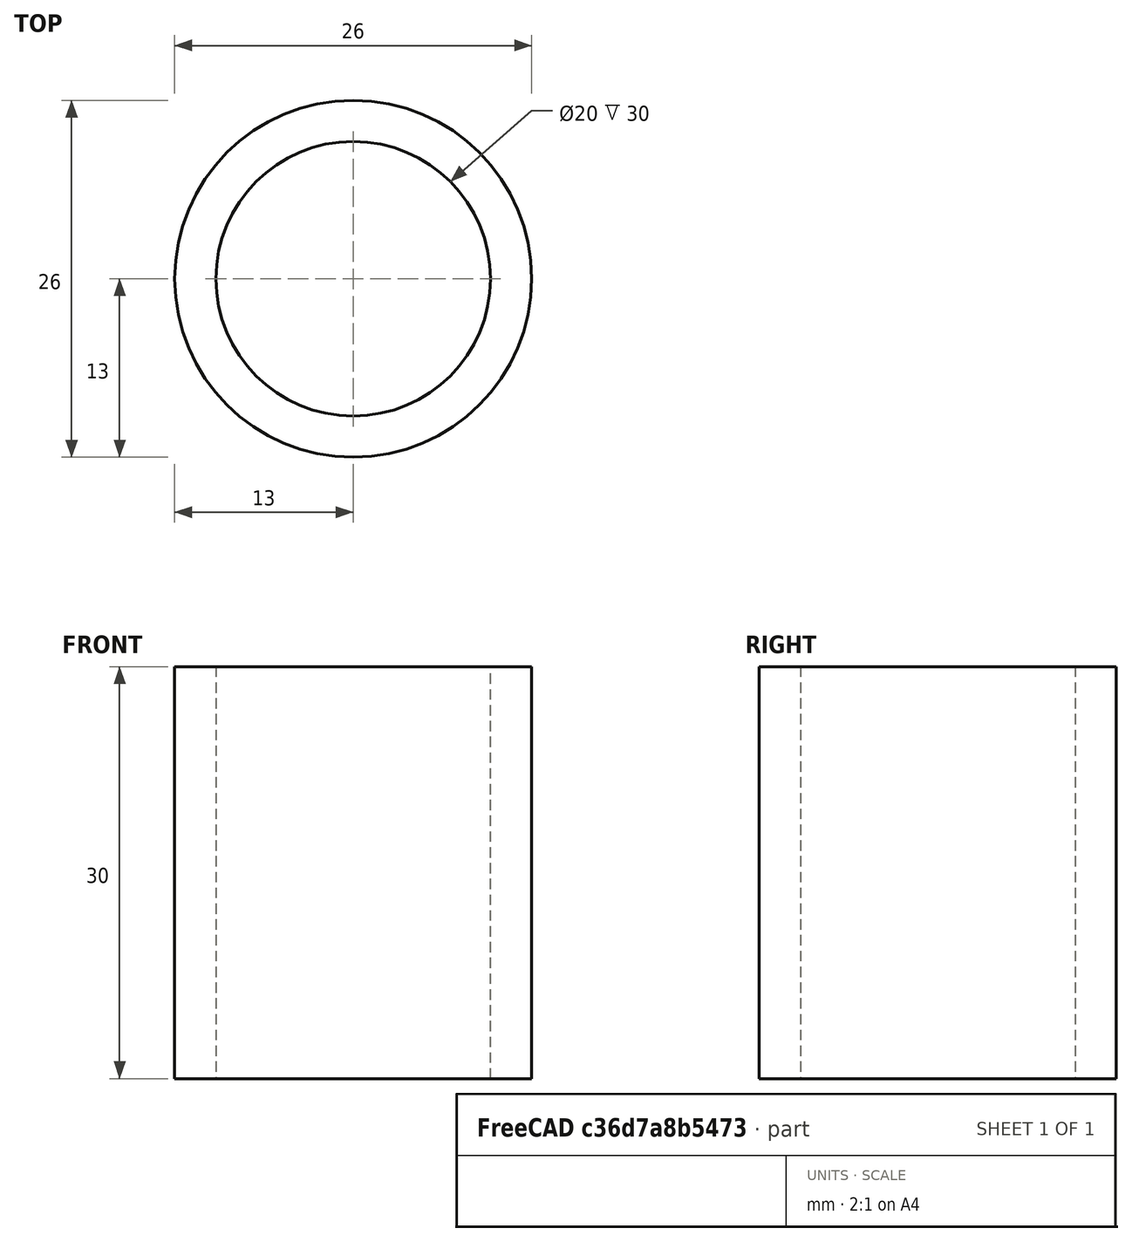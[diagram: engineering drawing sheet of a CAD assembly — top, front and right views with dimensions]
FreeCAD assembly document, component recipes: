
FREECAD ASSEMBLY — COMPONENT RECIPES ("Assembly_file")

This assembly document has 2 components, labeled P0..P1 below (a component is one placed body or linked part). 2 of them carry a construction recipe — the FreeCAD feature program that regenerates the part from scratch, quoted from this document or its linked companion documents; the rest are supplied as boundary geometry only. No exploded tour is included for this assembly.
COMPONENT P0 — recipe-attached ("Body_part_in", modeled in this document).
Construction recipe (the document's own serialized feature program — sketch geometry with constraints, then the solid features built on it; lengths are millimeters unless a unit is written):

FEATURE [Sketcher::SketchObject] Sketch
  FullyConstrained = true
  MapMode = 5
  Support = -> [XY_Plane001]
  sketch-geometry (1):
    g0: Circle CenterX=0 CenterY=0 CenterZ=0 NormalX=0 NormalY=0 NormalZ=1 AngleXU=0 Radius=10
  constraints (2):
    c: Coincident(g0,g-1)
    c: Diameter(g0) = 20
FEATURE [PartDesign::Pad] Pad
  Direction = (1,1,1)
  Length = 30
  Length2 = 100
  Profile = -> Sketch
  Type = 0
FEATURE [PartDesign::CoordinateSystem] LCS_in
  AttacherType = Attacher::AttachEngine3D
  MapMode = 11
  Placement = pos=(0,0,0) rot=(0,0,1;1.5708rad)
  Support = -> [Pad]
FEATURE [PartDesign::Body] Body  label="Body_part_in"
  Group = -> [Sketch,Pad,LCS_in]
  Origin = -> Origin001
  Tip = -> Pad
COMPONENT P1 — recipe-attached ("Body_part_out", modeled in this document).
Construction recipe (the document's own serialized feature program — sketch geometry with constraints, then the solid features built on it; lengths are millimeters unless a unit is written):

FEATURE [Sketcher::SketchObject] Sketch001
  FullyConstrained = true
  MapMode = 5
  Support = -> [XY_Plane002]
  sketch-geometry (1):
    g0: Circle CenterX=0 CenterY=0 CenterZ=0 NormalX=0 NormalY=0 NormalZ=1 AngleXU=0 Radius=10
  constraints (2):
    c: Coincident(g0,g-1)
    c: Diameter(g0) = 20
FEATURE [Sketcher::SketchObject] Sketch002
  FullyConstrained = true
  MapMode = 5
  Support = -> [XY_Plane002]
  sketch-geometry (1):
    g0: Circle CenterX=0 CenterY=0 CenterZ=0 NormalX=0 NormalY=0 NormalZ=1 AngleXU=0 Radius=13
  constraints (2):
    c: Coincident(g0,g-1)
    c: Diameter(g0) = 26
FEATURE [PartDesign::Pad] Pad001
  Direction = (1,1,1)
  Length = 30
  Length2 = 100
  Profile = -> Sketch002
  Type = 0
FEATURE [PartDesign::Pocket] Pocket
  BaseFeature = -> Pad001
  Length = 5
  Length2 = 100
  Profile = -> Sketch001
  Reversed = true
  Type = 1
FEATURE [PartDesign::CoordinateSystem] LCS_out
  AttacherType = Attacher::AttachEngine3D
  MapMode = 11
  Placement = pos=(0,0,0) rot=(0,0,1;1.5708rad)
  Support = -> [Pocket]
FEATURE [PartDesign::Body] Body001  label="Body_part_out"
  Group = -> [Sketch002,Pad001,Sketch001,Pocket,LCS_out]
  Origin = -> Origin002
  Tip = -> Pocket
PROVENANCE & LICENSES
A FreeCAD (.FCStd) document from a public repository crawl; recipes are the document's own serialized feature recipes (and, for linked parts, companion documents' recipes).
License: as declared in the source repository (recorded in the dataset sidecar).
